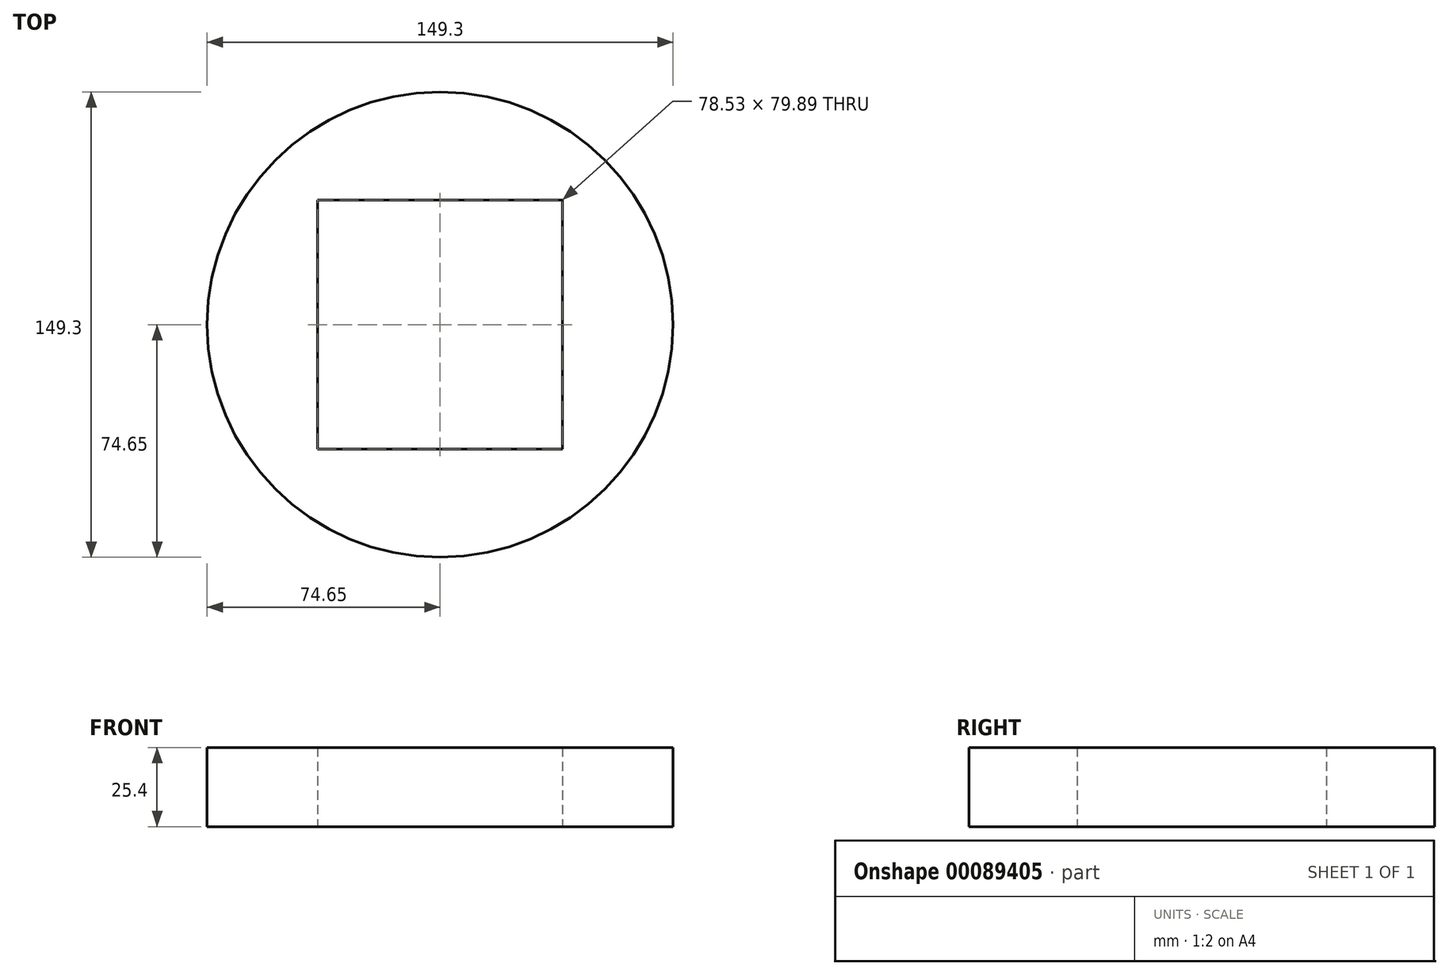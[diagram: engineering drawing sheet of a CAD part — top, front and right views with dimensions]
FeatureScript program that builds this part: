
annotation { "Feature Type Name" : "Feature", "Feature Type Description" : "" }
export const myFeature = defineFeature(function(context is Context, id is Id, definition is map)
    precondition{}
    {
        {
            var Q0;
            Q0=qCreatedBy(makeId("Top.planeOp"),FACE);
            var sketch = newSketch(context, id + "F0", { "sketchPlane" : qUnion([Q0])});
            skCircle(sketch, "E0", {"center": v(0, 0) * mm, "radius": 74.65 * mm});
            skLineSegment(sketch, "E1.bottom", {"start": v(39.26, 39.94) * mm, "end": v(-39.26, 39.94) * mm});
            skLineSegment(sketch, "E1.top", {"start": v(39.26, -39.94) * mm, "end": v(-39.26, -39.94) * mm});
            skLineSegment(sketch, "E1.left", {"start": v(39.26, 39.94) * mm, "end": v(39.26, -39.94) * mm});
            skLineSegment(sketch, "E1.right", {"start": v(-39.26, 39.94) * mm, "end": v(-39.26, -39.94) * mm});
            skSolve(sketch);
        }
        {
            var Q0;
            Q0=makeQuery(id+"F0.imprint","IMPRINT",FACE,{"disambiguationData":[TD([[makeQuery(id+"F0.imprint","IMPRINT",EDGE,{"derivedFrom":sQuery(id+"F0.wireOp",EDGE,"E0")}),1.0]])]});
            extrude(context, id + "F1", {"entities" : qUnion([Q0]), "depth" : 25.4 * mm});
        }
    });
